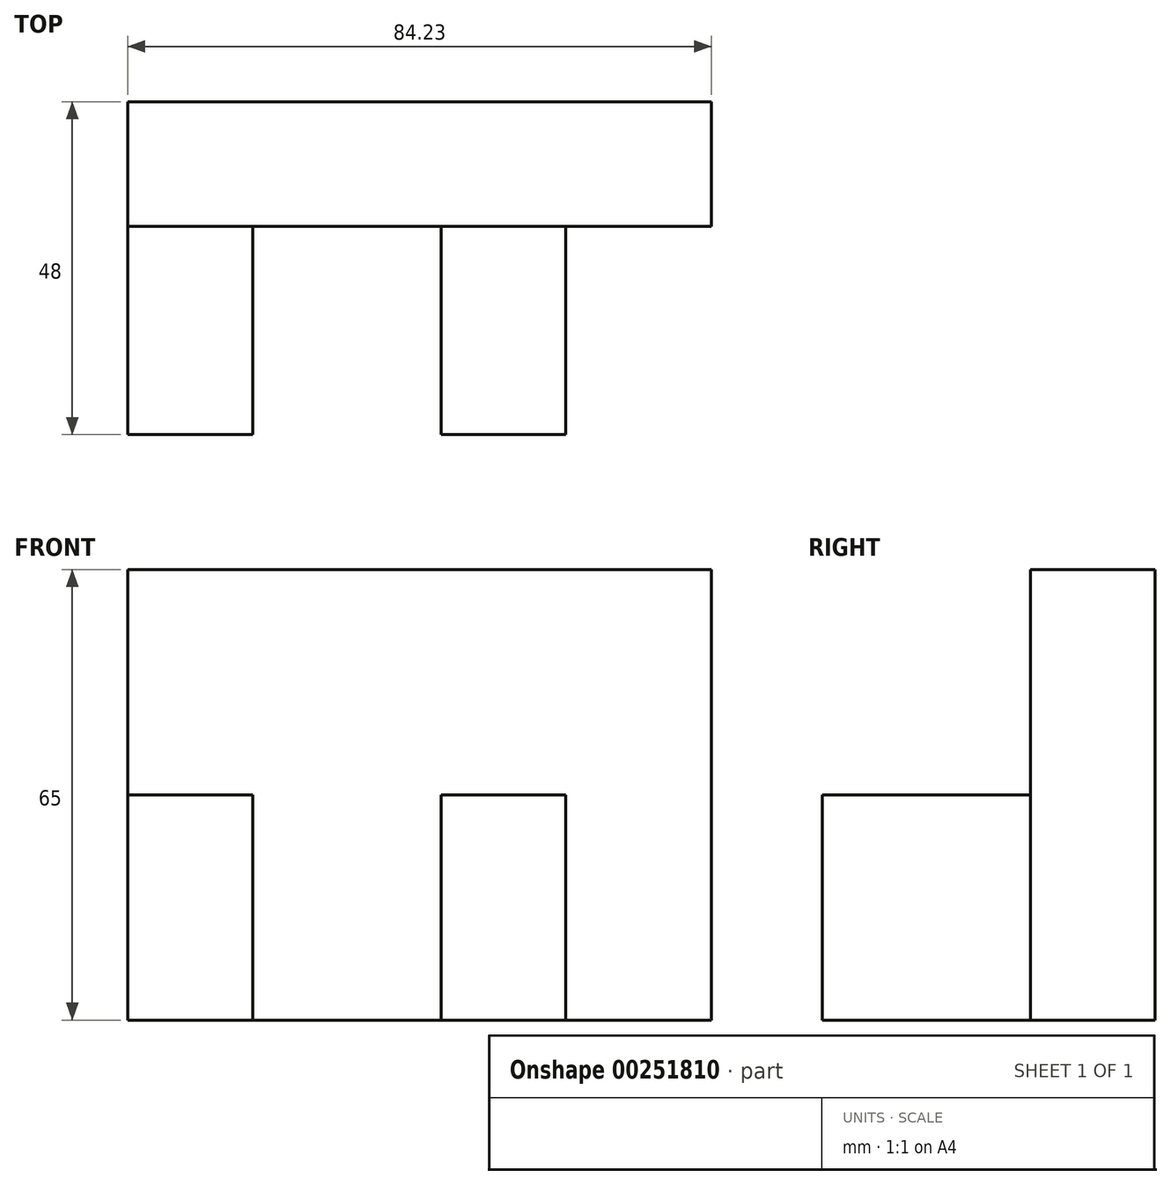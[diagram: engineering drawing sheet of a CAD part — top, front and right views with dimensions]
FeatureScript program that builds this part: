
annotation { "Feature Type Name" : "Feature", "Feature Type Description" : "" }
export const myFeature = defineFeature(function(context is Context, id is Id, definition is map)
    precondition{}
    {
        {
            var Q0;
            Q0=qCreatedBy(makeId("Front.planeOp"),FACE);
            var sketch = newSketch(context, id + "F0", { "sketchPlane" : qUnion([Q0])});
            skLineSegment(sketch, "E0.bottom", {"start": v(-50, 32.5) * mm, "end": v(50, 32.5) * mm});
            skLineSegment(sketch, "E0.top", {"start": v(-50, -32.5) * mm, "end": v(50, -32.5) * mm});
            skLineSegment(sketch, "E0.left", {"start": v(-50, 32.5) * mm, "end": v(-50, -32.5) * mm});
            skLineSegment(sketch, "E0.right", {"start": v(50, 32.5) * mm, "end": v(50, -32.5) * mm});
            skPoint(sketch, "E0.middle", {"position": v(0, 0) * mm});
            skSolve(sketch);
        }
        {
            var Q0;
            Q0=makeQuery(id+"F0.imprint","IMPRINT",FACE,{"disambiguationData":[TD([[makeQuery(id+"F0.imprint","IMPRINT",EDGE,{"derivedFrom":sQuery(id+"F0.wireOp",EDGE,"E0.bottom")}),-1.0]])]});
            extrude(context, id + "F1", {"entities" : qUnion([Q0]), "oppositeDirection" : true, "depth" : 18 * mm});
        }
        {
            var Q0;
            Q0=makeQuery(id+"F1.opExtrude","CAP_FACE",FACE,{"disambiguationData":[OSD([sQuery(id+"F0.wireOp",EDGE,"E0.bottom"),sQuery(id+"F0.wireOp",EDGE,"E0.top"),sQuery(id+"F0.wireOp",EDGE,"E0.left"),sQuery(id+"F0.wireOp",EDGE,"E0.right")])],"isStart":true});
            var sketch = newSketch(context, id + "F2", { "sketchPlane" : qUnion([Q0])});
            skLineSegment(sketch, "E1.bottom", {"start": v(10.97, 0) * mm, "end": v(28.97, 0) * mm});
            skLineSegment(sketch, "E1.top", {"start": v(10.97, -32.5) * mm, "end": v(28.97, -32.5) * mm});
            skLineSegment(sketch, "E1.left", {"start": v(10.97, 0) * mm, "end": v(10.97, -32.5) * mm});
            skLineSegment(sketch, "E1.right", {"start": v(28.97, 0) * mm, "end": v(28.97, -32.5) * mm});
            skLineSegment(sketch, "E2.bottom", {"start": v(-34.23, 0) * mm, "end": v(-16.23, 0) * mm});
            skLineSegment(sketch, "E2.top", {"start": v(-34.23, -32.5) * mm, "end": v(-16.23, -32.5) * mm});
            skLineSegment(sketch, "E2.left", {"start": v(-34.23, 0) * mm, "end": v(-34.23, -32.5) * mm});
            skLineSegment(sketch, "E2.right", {"start": v(-16.23, 0) * mm, "end": v(-16.23, -32.5) * mm});
            skSolve(sketch);
        }
        {
            var Q0;
            Q0=makeQuery(id+"F2.imprint","IMPRINT",FACE,{"disambiguationData":[TD([[makeQuery(id+"F2.imprint","IMPRINT",EDGE,{"derivedFrom":sQuery(id+"F2.wireOp",EDGE,"E2.bottom")}),-1.0]])]});
            extrude(context, id + "F3", {"entities" : qUnion([Q0]), "operationType" : NewBodyOperationType.ADD, "depth" : 30 * mm});
        }
        {
            var Q0;
            Q0=makeQuery(id+"F2.imprint","IMPRINT",FACE,{"disambiguationData":[TD([[makeQuery(id+"F2.imprint","IMPRINT",EDGE,{"derivedFrom":sQuery(id+"F2.wireOp",EDGE,"E1.bottom")}),-1.0]])]});
            extrude(context, id + "F4", {"entities" : qUnion([Q0]), "operationType" : NewBodyOperationType.ADD, "depth" : 30 * mm});
        }
        {
            var Q0;
            Q0=makeQuery(id+"F2.imprint","IMPRINT",FACE,{"disambiguationData":[TD([[makeQuery(id+"F2.imprint","IMPRINT",EDGE,{"derivedFrom":sQuery(id+"F2.wireOp",EDGE,"E1.bottom")}),1.0]])]});
            var sketch = newSketch(context, id + "F5", { "sketchPlane" : qUnion([Q0])});
            skLineSegment(sketch, "E3", {"start": v(-34.23, -32.42) * mm, "end": v(-34.23, 32.51) * mm});
            skLineSegment(sketch, "E4.0.8", {"start": v(-34.23, 32.5) * mm, "end": v(-50, 32.5) * mm});
            skLineSegment(sketch, "E4.0.9", {"start": v(-50, 32.5) * mm, "end": v(-50, -32.5) * mm});
            skLineSegment(sketch, "E4.0.10", {"start": v(-50, -32.5) * mm, "end": v(-34.23, -32.5) * mm});
            skLineSegment(sketch, "E4.0.11", {"start": v(-34.23, -32.5) * mm, "end": v(-34.23, 0) * mm});
            skPoint(sketch, "E4.0.7.end.orphan", {"position": v(50, 32.5) * mm});
            skPoint(sketch, "E4.0.6.end.orphan", {"position": v(50, -32.5) * mm});
            skPoint(sketch, "E4.0.5.end.orphan", {"position": v(28.97, -32.5) * mm});
            skPoint(sketch, "E4.0.4.end.orphan", {"position": v(28.97, 0) * mm});
            skPoint(sketch, "E4.0.3.end.orphan", {"position": v(10.97, 0) * mm});
            skPoint(sketch, "E4.0.2.end.orphan", {"position": v(10.97, -32.5) * mm});
            skPoint(sketch, "E4.0.1.end.orphan", {"position": v(-16.23, -32.5) * mm});
            skPoint(sketch, "E4.0.0.end.orphan", {"position": v(-16.23, 0) * mm});
            skSolve(sketch);
        }
        {
            var Q0;
            Q0 = qSketchRegion(id + "F5", true);
            extrude(context, id + "F6", {"entities" : qUnion([Q0]), "operationType" : NewBodyOperationType.ADD, "depth" : 25 * mm});
        }
        {
            var Q0;
            Q0=makeQuery(id+"F6.opExtrude","CAP_FACE",FACE,{"disambiguationData":[OSD([sQuery(id+"F5.wireOp",EDGE,"E3"),sQuery(id+"F5.wireOp",EDGE,"E4.0.8"),sQuery(id+"F5.wireOp",EDGE,"E4.0.9"),sQuery(id+"F5.wireOp",EDGE,"E4.0.10"),sQuery(id+"F5.wireOp",EDGE,"E4.0.11")])],"isStart":false});
            extrude(context, id + "F7", {"entities" : qUnion([Q0]), "operationType" : NewBodyOperationType.REMOVE, "oppositeDirection" : true, "depth" : 43 * mm});
        }
    });
